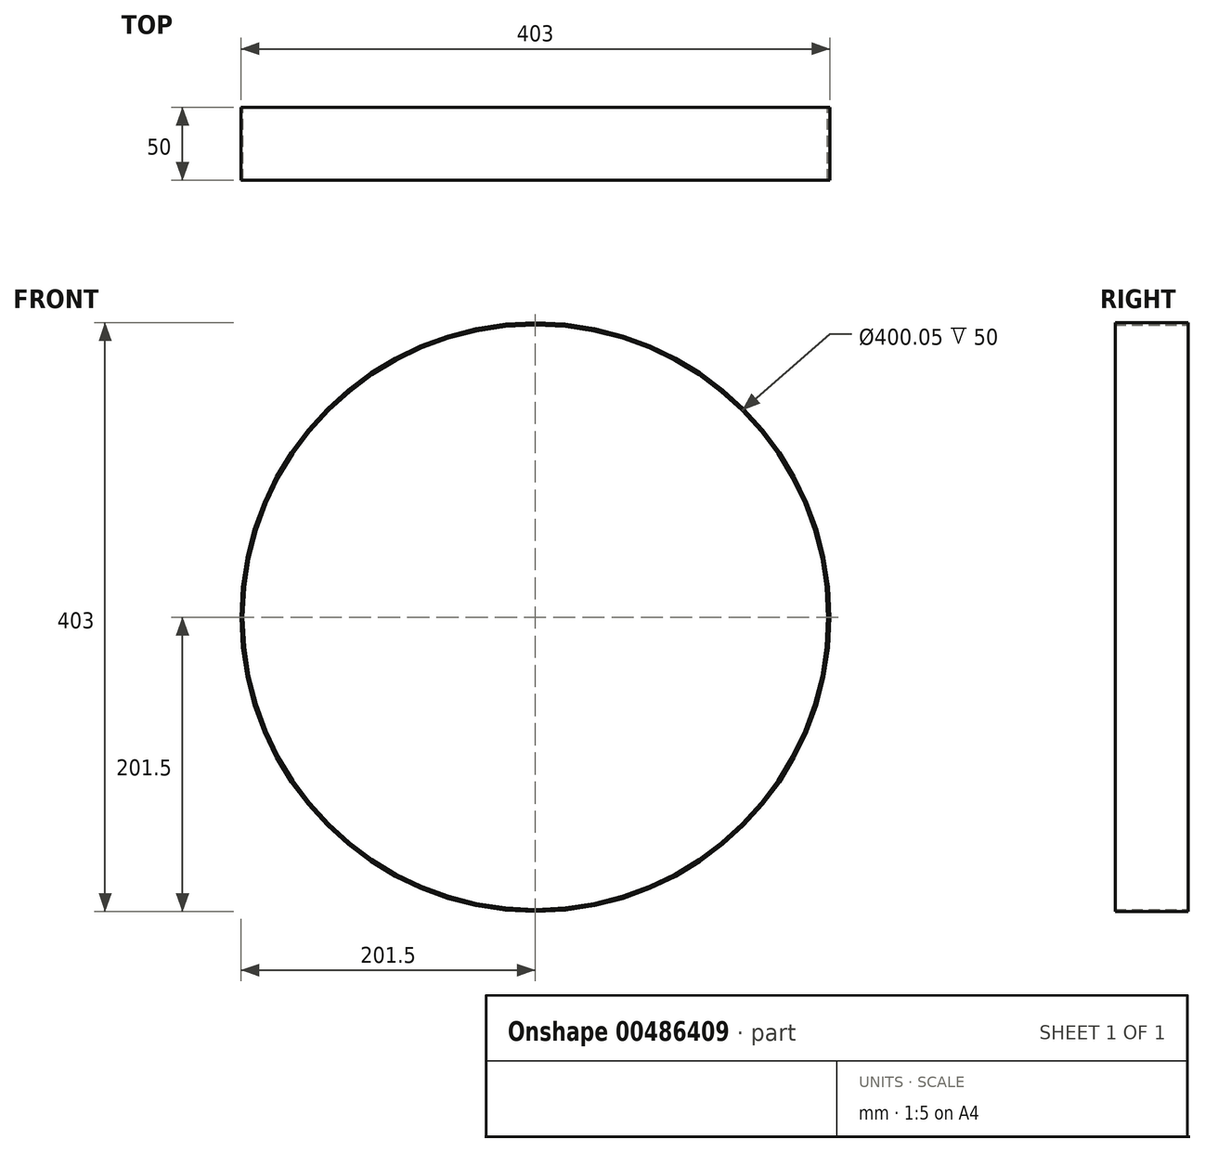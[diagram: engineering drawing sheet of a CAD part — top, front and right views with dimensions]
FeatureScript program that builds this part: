
annotation { "Feature Type Name" : "Feature", "Feature Type Description" : "" }
export const myFeature = defineFeature(function(context is Context, id is Id, definition is map)
    precondition{}
    {
        {
            var Q0;
            Q0=qCreatedBy(makeId("Front.planeOp"),FACE);
            var sketch = newSketch(context, id + "F0", { "sketchPlane" : qUnion([Q0])});
            skCircle(sketch, "E0", {"center": v(0, 0) * mm, "radius": 201.5 * mm});
            skCircle(sketch, "E1", {"center": v(0, 0) * mm, "radius": 200.03 * mm});
            skSolve(sketch);
        }
        {
            var Q0;
            Q0=makeQuery(id+"F0.imprint","IMPRINT",FACE,{"disambiguationData":[TD([[makeQuery(id+"F0.imprint","IMPRINT",EDGE,{"derivedFrom":sQuery(id+"F0.wireOp",EDGE,"E0")}),1.0]])]});
            extrude(context, id + "F1", {"entities" : qUnion([Q0]), "depth" : 50 * mm});
        }
    });
